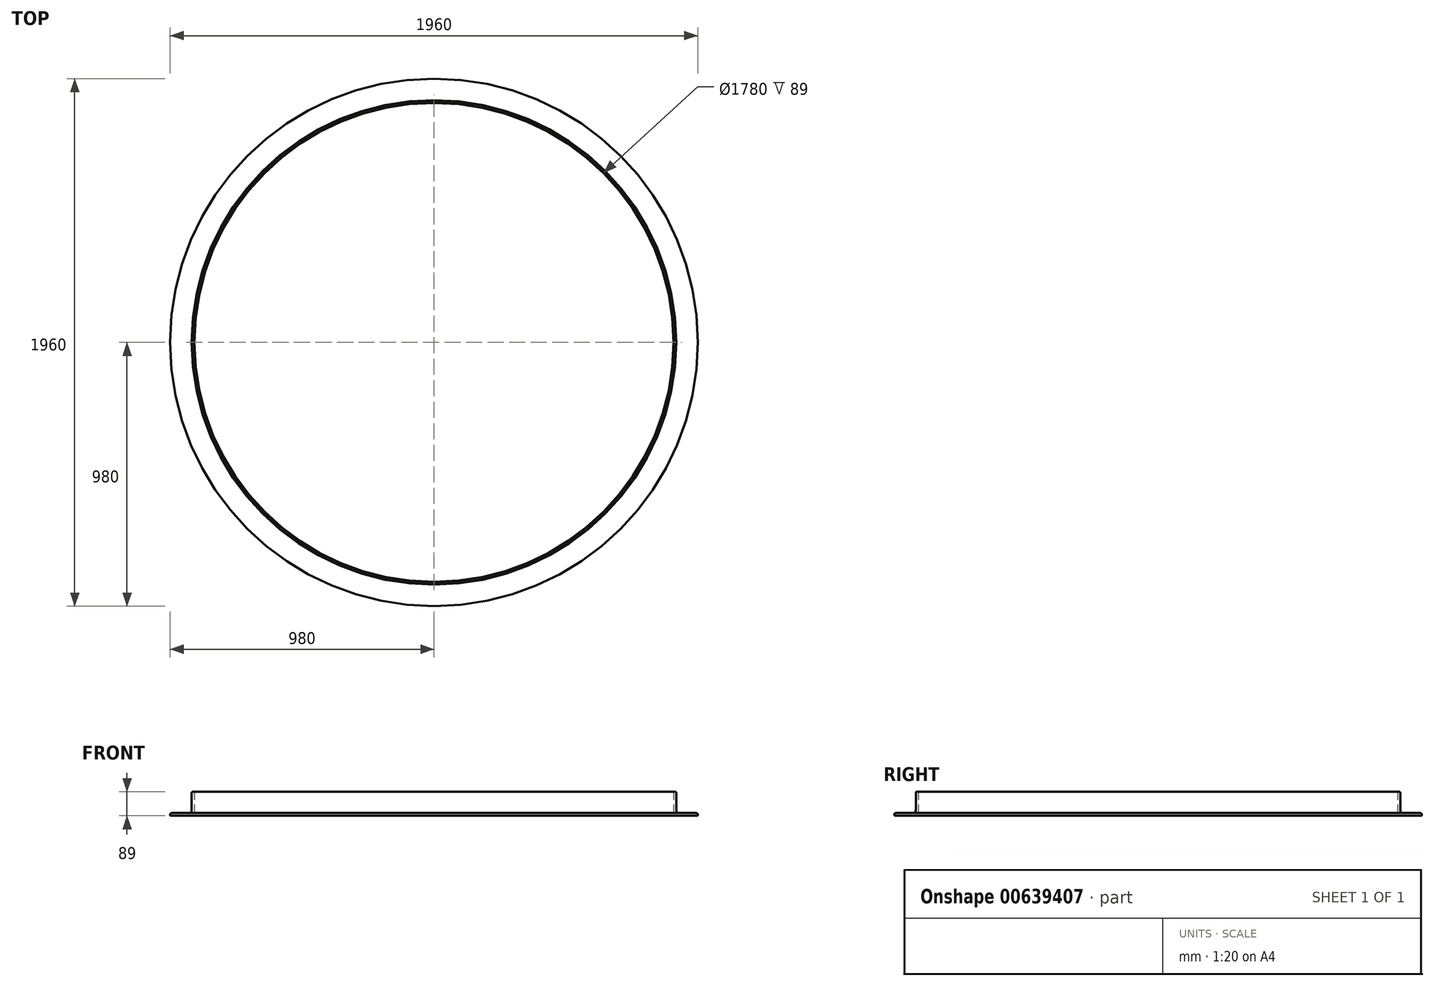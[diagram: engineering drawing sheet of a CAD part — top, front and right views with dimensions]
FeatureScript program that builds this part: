
annotation { "Feature Type Name" : "Feature", "Feature Type Description" : "" }
export const myFeature = defineFeature(function(context is Context, id is Id, definition is map)
    precondition{}
    {
        {
            var Q0;
            Q0=qCreatedBy(makeId("Right.planeOp"),FACE);
            var sketch = newSketch(context, id + "F0", { "sketchPlane" : qUnion([Q0])});
            skLineSegment(sketch, "E0", {"start": v(0, 90) * mm, "end": v(0, 0) * mm});
            skLineSegment(sketch, "E1", {"start": v(0, 0) * mm, "end": v(90, 0) * mm});
            skLineSegment(sketch, "E2.0", {"start": v(21, 10) * mm, "end": v(84.5, 10) * mm});
            skLineSegment(sketch, "E2.1", {"start": v(10, 84.5) * mm, "end": v(10, 21) * mm});
            skLineSegment(sketch, "E3", {"start": v(0, 90) * mm, "end": v(4.5, 90) * mm});
            skLineSegment(sketch, "E4", {"start": v(90, 4.5) * mm, "end": v(90, 0) * mm});
            skPoint(sketch, "E5.visualSharp", {"position": v(10, 10) * mm});
            skArc(sketch, "E5.filletArc", {"start": v(10, 21) * mm, "mid": v(13.22, 13.22) * mm, "end": v(21, 10) * mm});
            skPoint(sketch, "E6.visualSharp", {"position": v(10, 90) * mm});
            skArc(sketch, "E6.filletArc", {"start": v(10, 84.5) * mm, "mid": v(8.39, 88.39) * mm, "end": v(4.5, 90) * mm});
            skPoint(sketch, "E7.visualSharp", {"position": v(90, 10) * mm});
            skArc(sketch, "E7.filletArc", {"start": v(90, 4.5) * mm, "mid": v(88.39, 8.39) * mm, "end": v(84.5, 10) * mm});
            skLineSegment(sketch, "E8", {"start": v(-890, -85.95) * mm, "end": v(-890, 171.99) * mm, "construction": true});
            skSolve(sketch);
        }
        {
            var Q0;
            Q0=makeQuery(id+"F0.imprint","IMPRINT",FACE,{"disambiguationData":[TD([[makeQuery(id+"F0.imprint","IMPRINT",EDGE,{"derivedFrom":sQuery(id+"F0.wireOp",EDGE,"E0")}),1.0]])]});
            var Q1;
            Q1=sQuery(id+"F0.wireOp",EDGE,"E8");
            revolve(context, id + "F1", {"entities" : qUnion([Q0]), "axis" : qUnion([Q1]), "revolveType" : RevolveType.FULL});
        }
        {
            var Q0;
            Q0=qCreatedBy(makeId("Right.planeOp"),FACE);
            var sketch = newSketch(context, id + "F2", { "sketchPlane" : qUnion([Q0])});
            skLineSegment(sketch, "E9.bottom", {"start": v(79.25, 89) * mm, "end": v(-1874.52, 89) * mm});
            skLineSegment(sketch, "E9.top", {"start": v(79.25, 116.22) * mm, "end": v(-1874.52, 116.22) * mm});
            skLineSegment(sketch, "E9.left", {"start": v(79.25, 89) * mm, "end": v(79.25, 116.22) * mm});
            skLineSegment(sketch, "E9.right", {"start": v(-1874.52, 89) * mm, "end": v(-1874.52, 116.22) * mm});
            skSolve(sketch);
        }
        {
            var Q0;
            Q0=makeQuery(id+"F2.imprint","IMPRINT",FACE,{"disambiguationData":[TD([[makeQuery(id+"F2.imprint","IMPRINT",EDGE,{"derivedFrom":sQuery(id+"F2.wireOp",EDGE,"E9.bottom")}),-1.0]])]});
            extrude(context, id + "F3", {"entities" : qUnion([Q0]), "operationType" : NewBodyOperationType.REMOVE, "oppositeDirection" : true, "depth" : 1800 * mm, "offsetDistance" : 25 * mm, "symmetric" : true});
        }
    });
